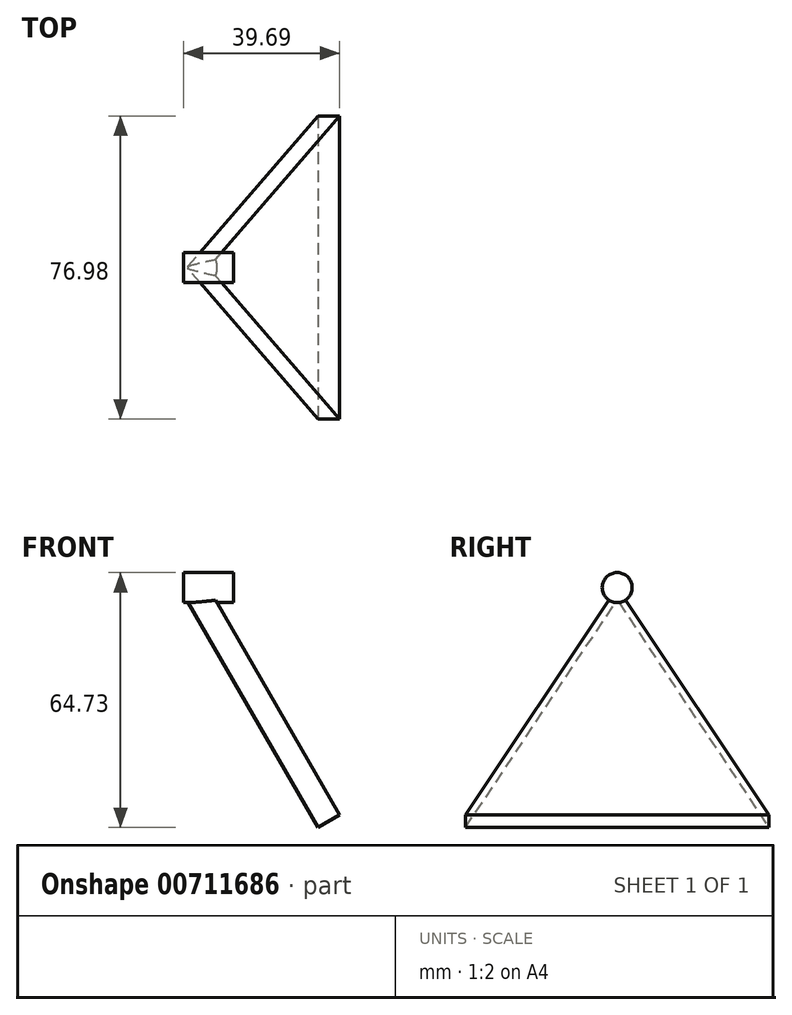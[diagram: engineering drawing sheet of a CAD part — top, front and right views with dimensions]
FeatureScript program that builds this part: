
annotation { "Feature Type Name" : "Feature", "Feature Type Description" : "" }
export const myFeature = defineFeature(function(context is Context, id is Id, definition is map)
    precondition{}
    {
        {
            var Q0;
            Q0=qCreatedBy(makeId("Top.planeOp"),FACE);
            var sketch = newSketch(context, id + "F0", { "sketchPlane" : qUnion([Q0])});
            skArc(sketch, "E0", {"start": v(0, 0) * mm, "mid": v(2.6, -19.72) * mm, "end": v(10.2, -38.1) * mm});
            skLineSegment(sketch, "E1", {"start": v(10.2, -38.1) * mm, "end": v(76.2, 0) * mm, "construction": true});
            skSolve(sketch);
        }
        {
            var Q0;
            Q0=qCreatedBy(makeId("Right.planeOp"),FACE);
            cPlane(context, id + "F1", {"entities" : qUnion([Q0]), "cplaneType" : CPlaneType.OFFSET, "offset" : 12.7 * mm, "oppositeDirection" : true, "width" : 152.4 * mm, "height" : 152.4 * mm});
        }
        {
            var Q0;
            Q0=qCreatedBy(id+"F1.planeOp",FACE);
            var sketch = newSketch(context, id + "F2", { "sketchPlane" : qUnion([Q0])});
            skCircle(sketch, "E2", {"center": v(0, 0) * mm, "radius": 3.81 * mm});
            skSolve(sketch);
        }
        {
            var Q0;
            Q0=qCreatedBy(makeId("Front.planeOp"),FACE);
            var sketch = newSketch(context, id + "F3", { "sketchPlane" : qUnion([Q0])});
            skLineSegment(sketch, "E3", {"start": v(-12.7, 0) * mm, "end": v(9.53, -38.5) * mm, "construction": true});
            skLineSegment(sketch, "E4", {"start": v(9.53, -38.5) * mm, "end": v(76.2, 0) * mm, "construction": true});
            skSolve(sketch);
        }
        {
            var Q0;
            Q0=sQuery(id+"F3.wireOp",EDGE,"E3");
            var Q1;
            Q1=qCreatedBy(makeId("Front.planeOp"),FACE);
            cPlane(context, id + "F4", {"entities" : qUnion([Q0, Q1]), "cplaneType" : CPlaneType.LINE_ANGLE, "offset" : 25.4 * mm, "angle" : 90 * degree, "width" : 152.4 * mm, "height" : 152.4 * mm});
        }
        {
            var Q0;
            Q0=qCreatedBy(id+"F4.planeOp",FACE);
            var sketch = newSketch(context, id + "F5", { "sketchPlane" : qUnion([Q0])});
            skCircle(sketch, "E5.cCircle", {"center": v(0, -38.1) * mm, "radius": 22.23 * mm, "construction": true});
            skLineSegment(sketch, "E5.0", {"start": v(0, 6.35) * mm, "end": v(38.5, -60.33) * mm});
            skLineSegment(sketch, "E5.1", {"start": v(38.5, -60.33) * mm, "end": v(-38.5, -60.33) * mm});
            skLineSegment(sketch, "E5.2", {"start": v(-38.5, -60.33) * mm, "end": v(0, 6.35) * mm});
            skPoint(sketch, "E5.0.midPoint", {"position": v(19.25, -26.99) * mm});
            skSolve(sketch);
        }
        {
            var Q0;
            Q0=makeQuery(id+"F2.imprint","IMPRINT",FACE,{"disambiguationData":[TD([[makeQuery(id+"F2.imprint","IMPRINT",EDGE,{"derivedFrom":sQuery(id+"F2.wireOp",EDGE,"E2")}),1.0]])]});
            var Q1;
            Q1=sQuery(id+"F2.wireOp",EDGE,"E2");
            extrude(context, id + "F6", {"entities" : qUnion([Q0]), "surfaceEntities" : qUnion([Q1]), "endBound" : BoundingType.SYMMETRIC, "depth" : 12.7 * mm, "offsetDistance" : 25.4 * mm});
        }
        {
            var Q0;
            Q0 = qSketchRegion(id + "F5", true);
            extrude(context, id + "F7", {"entities" : qUnion([Q0]), "operationType" : NewBodyOperationType.ADD, "oppositeDirection" : true, "depth" : 6.35 * mm, "offsetDistance" : 25.4 * mm});
        }
    });
